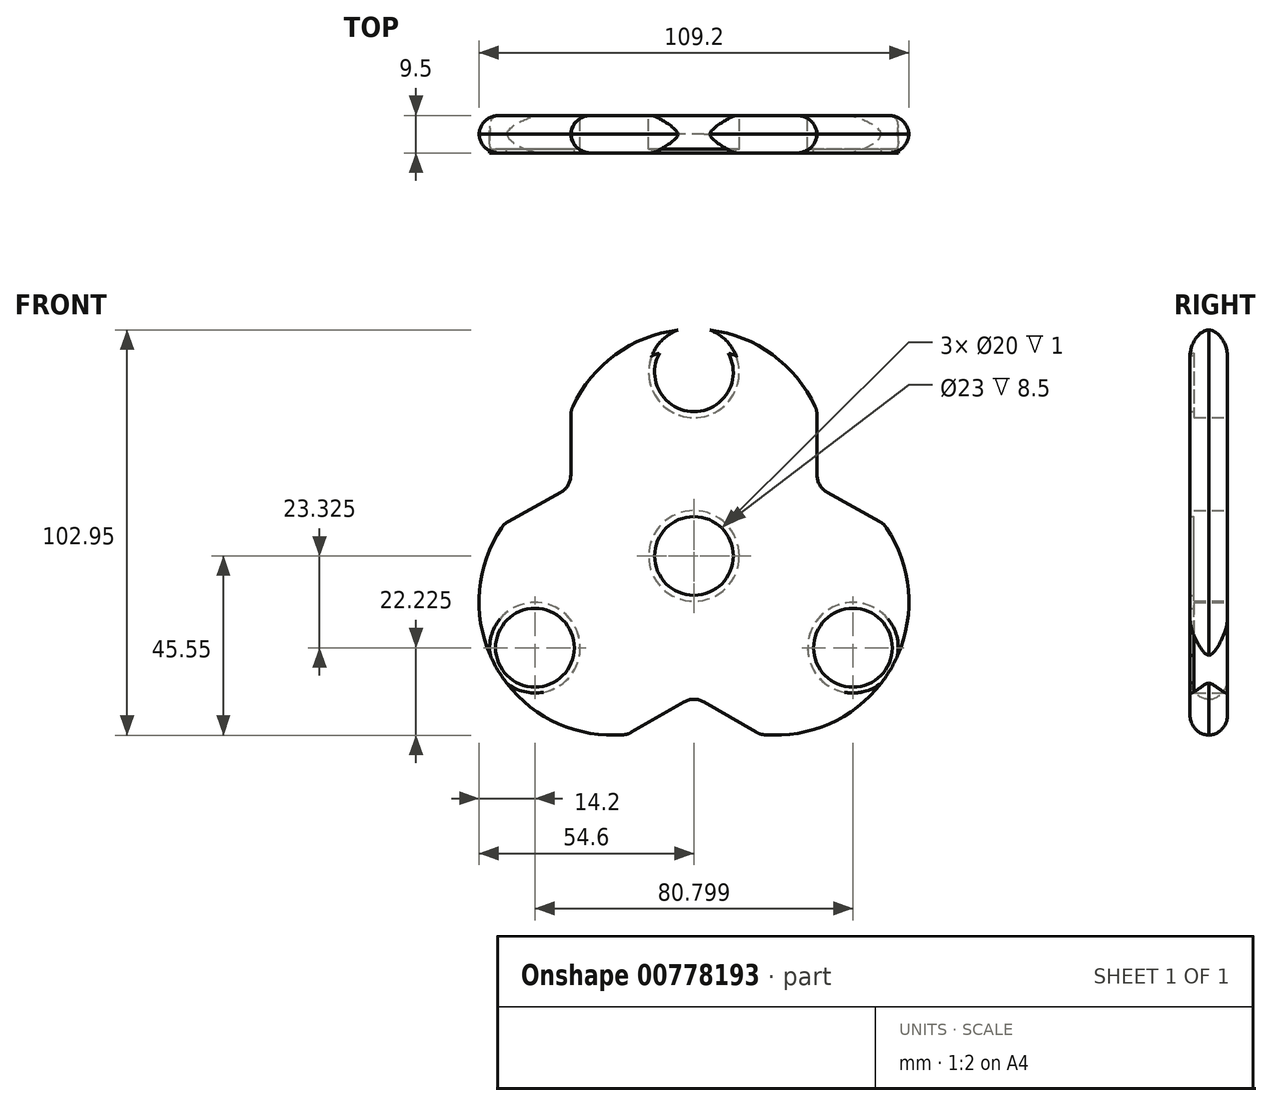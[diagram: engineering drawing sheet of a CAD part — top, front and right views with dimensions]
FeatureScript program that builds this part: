
annotation { "Feature Type Name" : "Feature", "Feature Type Description" : "" }
export const myFeature = defineFeature(function(context is Context, id is Id, definition is map)
    precondition{}
    {
        {
            var Q0;
            Q0=qCreatedBy(makeId("Front.planeOp"),FACE);
            var sketch = newSketch(context, id + "F0", { "sketchPlane" : qUnion([Q0])});
            skCircle(sketch, "E0", {"center": v(0, 0) * mm, "radius": 11.5 * mm});
            skPoint(sketch, "E1", {"position": v(-31.25, 36.9) * mm});
            skPoint(sketch, "E2", {"position": v(31.25, 36.9) * mm});
            skArc(sketch, "E3", {"start": v(30.8, 37.93) * mm, "mid": v(0, 57.65) * mm, "end": v(-30.8, 37.93) * mm});
            skPoint(sketch, "E4", {"position": v(-16.74, -45.31) * mm});
            skPoint(sketch, "E5", {"position": v(16.74, -45.31) * mm});
            skPoint(sketch, "E6", {"position": v(48.18, 8.2) * mm});
            skPoint(sketch, "E7", {"position": v(-48.18, 8.2) * mm});
            skArc(sketch, "E8", {"start": v(-48.9, 7.16) * mm, "mid": v(-49.9, -28.87) * mm, "end": v(-17.9, -45.43) * mm});
            skArc(sketch, "E9", {"start": v(17.9, -45.43) * mm, "mid": v(49.9, -28.87) * mm, "end": v(48.9, 7.16) * mm});
            skPoint(sketch, "E10", {"position": v(0, -35.66) * mm});
            skPoint(sketch, "E11", {"position": v(-31.3, 17.57) * mm});
            skPoint(sketch, "E12", {"position": v(31.3, 17.57) * mm});
            skLineSegment(sketch, "E13", {"start": v(2.5, -37.1) * mm, "end": v(15.8, -44.78) * mm});
            skLineSegment(sketch, "E14", {"start": v(-33.86, 16.15) * mm, "end": v(-47.17, 8.76) * mm});
            skLineSegment(sketch, "E15", {"start": v(-2.5, -37.1) * mm, "end": v(-15.8, -44.78) * mm});
            skLineSegment(sketch, "E16", {"start": v(-31.25, 35.85) * mm, "end": v(-31.29, 20.5) * mm});
            skLineSegment(sketch, "E17", {"start": v(31.25, 35.85) * mm, "end": v(31.29, 20.5) * mm});
            skLineSegment(sketch, "E18", {"start": v(47.17, 8.76) * mm, "end": v(33.86, 16.15) * mm});
            skCircle(sketch, "E19", {"center": v(-40.4, -23.32) * mm, "radius": 11.5 * mm});
            skCircle(sketch, "E20", {"center": v(0, 46.65) * mm, "radius": 11.5 * mm});
            skCircle(sketch, "E21", {"center": v(40.4, -23.32) * mm, "radius": 11.5 * mm});
            skPoint(sketch, "E22", {"position": v(-49.93, -28.82) * mm});
            skPoint(sketch, "E23", {"position": v(0, 57.65) * mm});
            skPoint(sketch, "E24", {"position": v(49.93, -28.82) * mm});
            skArc(sketch, "E25.filletArc", {"start": v(-30.8, 37.93) * mm, "mid": v(-31.13, 36.91) * mm, "end": v(-31.25, 35.85) * mm});
            skArc(sketch, "E26.filletArc", {"start": v(31.25, 35.85) * mm, "mid": v(31.13, 36.91) * mm, "end": v(30.8, 37.93) * mm});
            skArc(sketch, "E27.filletArc", {"start": v(48.9, 7.16) * mm, "mid": v(48.13, 8.06) * mm, "end": v(47.17, 8.76) * mm});
            skArc(sketch, "E28.filletArc", {"start": v(15.8, -44.78) * mm, "mid": v(16.81, -45.22) * mm, "end": v(17.9, -45.43) * mm});
            skArc(sketch, "E29.filletArc", {"start": v(-17.9, -45.43) * mm, "mid": v(-16.81, -45.22) * mm, "end": v(-15.8, -44.78) * mm});
            skArc(sketch, "E30.filletArc", {"start": v(-47.17, 8.76) * mm, "mid": v(-48.13, 8.06) * mm, "end": v(-48.9, 7.16) * mm});
            skArc(sketch, "E31.filletArc", {"start": v(2.5, -37.1) * mm, "mid": v(0, -36.43) * mm, "end": v(-2.5, -37.1) * mm});
            skArc(sketch, "E32.filletArc", {"start": v(31.29, 20.5) * mm, "mid": v(31.98, 17.98) * mm, "end": v(33.86, 16.15) * mm});
            skArc(sketch, "E33.filletArc", {"start": v(-33.86, 16.15) * mm, "mid": v(-31.98, 17.98) * mm, "end": v(-31.29, 20.5) * mm});
            skSolve(sketch);
        }
        {
            var Q0;
            Q0=makeQuery(id+"F0.imprint","IMPRINT",FACE,{"disambiguationData":[TD([[makeQuery(id+"F0.imprint","IMPRINT",EDGE,{"derivedFrom":sQuery(id+"F0.wireOp",EDGE,"E0")}),-1.0]])]});
            extrude(context, id + "F1", {"entities" : qUnion([Q0]), "depth" : 4.75 * mm, "offsetDistance" : 25 * mm});
        }
        {
            var Q0;
            {var subQ0=sQuery(id+"F0.wireOp",EDGE,"E8");Q0=makeQuery(id+"F1.opExtrude","CAP_EDGE",EDGE,{"disambiguationData":[OSD([subQ0]),TDD([makeQuery(id+"F0.imprint","IMPRINT",EDGE,{"disambiguationData":[TD([[makeQuery(id+"F0.imprint","INTERSECT",VERTEX,{"derivedFrom":[subQ0,sQuery(id+"F0.wireOp",EDGE,"E29.filletArc")]}),1.0]])],"derivedFrom":subQ0})])],"isStart":false});}
            var Q1;
            {var subQ0=sQuery(id+"F0.wireOp",EDGE,"E8");Q1=makeQuery(id+"F1.opExtrude","CAP_EDGE",EDGE,{"disambiguationData":[OSD([subQ0]),TDD([makeQuery(id+"F0.imprint","IMPRINT",EDGE,{"disambiguationData":[TD([[makeQuery(id+"F0.imprint","INTERSECT",VERTEX,{"derivedFrom":[subQ0,sQuery(id+"F0.wireOp",EDGE,"E30.filletArc")]}),-1.0]])],"derivedFrom":subQ0})])],"isStart":false});}
            var Q2;
            Q2=makeQuery(id+"F1.opExtrude","CAP_EDGE",EDGE,{"disambiguationData":[OSD([sQuery(id+"F0.wireOp",EDGE,"E17")])],"isStart":false});
            fillet(context, id + "F2", {"entities" : qUnion([Q0, Q1, Q2]), "radius" : 5 * mm, "tangentPropagation" : true, "allowEdgeOverflow" : false});
        }
        {
            var Q0;
            Q0=makeQuery(id+"F1.opExtrude","SWEPT_BODY",BODY,{"disambiguationData":[OSD([sQuery(id+"F0.wireOp",EDGE,"E0"),sQuery(id+"F0.wireOp",EDGE,"E3"),sQuery(id+"F0.wireOp",EDGE,"E8"),sQuery(id+"F0.wireOp",EDGE,"E9"),sQuery(id+"F0.wireOp",EDGE,"E13"),sQuery(id+"F0.wireOp",EDGE,"E14"),sQuery(id+"F0.wireOp",EDGE,"E15"),sQuery(id+"F0.wireOp",EDGE,"E16"),sQuery(id+"F0.wireOp",EDGE,"E17"),sQuery(id+"F0.wireOp",EDGE,"E18"),sQuery(id+"F0.wireOp",EDGE,"E19"),sQuery(id+"F0.wireOp",EDGE,"E20"),sQuery(id+"F0.wireOp",EDGE,"E21"),sQuery(id+"F0.wireOp",EDGE,"E25.filletArc"),sQuery(id+"F0.wireOp",EDGE,"E26.filletArc"),sQuery(id+"F0.wireOp",EDGE,"E27.filletArc"),sQuery(id+"F0.wireOp",EDGE,"E28.filletArc"),sQuery(id+"F0.wireOp",EDGE,"E29.filletArc"),sQuery(id+"F0.wireOp",EDGE,"E30.filletArc"),sQuery(id+"F0.wireOp",EDGE,"E31.filletArc"),sQuery(id+"F0.wireOp",EDGE,"E32.filletArc"),sQuery(id+"F0.wireOp",EDGE,"E33.filletArc")])]});
            var Q1;
            Q1=qCreatedBy(makeId("Front.planeOp"),FACE);
            mirror(context, id + "F3", {"operationType" : NewBodyOperationType.ADD, "entities" : qUnion([Q0]), "mirrorPlane" : qUnion([Q1])});
        }
        {
            var Q0;
            Q0=qCreatedBy(makeId("Front.planeOp"),FACE);
            var sketch = newSketch(context, id + "F4", { "sketchPlane" : qUnion([Q0])});
            skCircle(sketch, "E34.cCircle", {"center": v(0, 0) * mm, "radius": 11.66 * mm, "construction": true});
            skLineSegment(sketch, "E34.0", {"start": v(20.2, -11.66) * mm, "end": v(-20.2, -11.66) * mm});
            skLineSegment(sketch, "E34.1", {"start": v(-20.2, -11.66) * mm, "end": v(0, 23.33) * mm});
            skLineSegment(sketch, "E34.2", {"start": v(0, 23.32) * mm, "end": v(20.2, -11.66) * mm});
            skPoint(sketch, "E34.0.midPoint", {"position": v(0, -11.66) * mm});
            skSolve(sketch);
        }
        {
            var Q0;
            Q0=qCreatedBy(makeId("Front.planeOp"),FACE);
            var sketch = newSketch(context, id + "F5", { "sketchPlane" : qUnion([Q0])});
            skCircle(sketch, "E35", {"center": v(0, 0) * mm, "radius": 11.5 * mm});
            skArc(sketch, "E36", {"start": v(30.8, 37.93) * mm, "mid": v(0, 57.65) * mm, "end": v(-30.8, 37.93) * mm});
            skArc(sketch, "E37", {"start": v(-48.9, 7.16) * mm, "mid": v(-49.9, -28.87) * mm, "end": v(-17.9, -45.43) * mm});
            skArc(sketch, "E38", {"start": v(17.9, -45.43) * mm, "mid": v(49.9, -28.87) * mm, "end": v(48.9, 7.16) * mm});
            skCircle(sketch, "E39", {"center": v(-40.4, -23.32) * mm, "radius": 11.5 * mm});
            skCircle(sketch, "E40", {"center": v(0, 46.65) * mm, "radius": 11.5 * mm});
            skCircle(sketch, "E41", {"center": v(40.4, -23.32) * mm, "radius": 11.5 * mm});
            skPoint(sketch, "E42", {"position": v(-49.93, -28.82) * mm});
            skPoint(sketch, "E43", {"position": v(0, 57.65) * mm});
            skPoint(sketch, "E44", {"position": v(49.93, -28.82) * mm});
            skCircle(sketch, "E45", {"center": v(-40.4, -23.32) * mm, "radius": 10 * mm});
            skCircle(sketch, "E46", {"center": v(0, 0) * mm, "radius": 10 * mm});
            skCircle(sketch, "E47", {"center": v(0, 46.65) * mm, "radius": 10 * mm});
            skCircle(sketch, "E48", {"center": v(40.4, -23.32) * mm, "radius": 10 * mm});
            skArc(sketch, "E49", {"start": v(30.8, 32.93) * mm, "mid": v(0, 52.65) * mm, "end": v(-30.8, 32.93) * mm});
            skPoint(sketch, "E50", {"position": v(0, 52.65) * mm});
            skSolve(sketch);
        }
        {
            var Q0;
            Q0=makeQuery(id+"F5.imprint","IMPRINT",FACE,{"disambiguationData":[TD([[makeQuery(id+"F5.imprint","IMPRINT",EDGE,{"derivedFrom":sQuery(id+"F5.wireOp",EDGE,"E35")}),1.0]])]});
            var Q1;
            Q1=makeQuery(id+"F5.imprint","IMPRINT",FACE,{"disambiguationData":[TD([[makeQuery(id+"F5.imprint","IMPRINT",EDGE,{"derivedFrom":sQuery(id+"F5.wireOp",EDGE,"E47")}),-1.0]])]});
            var Q2;
            Q2=makeQuery(id+"F5.imprint","IMPRINT",FACE,{"disambiguationData":[TD([[makeQuery(id+"F5.imprint","IMPRINT",EDGE,{"derivedFrom":sQuery(id+"F5.wireOp",EDGE,"E45")}),-1.0]])]});
            var Q3;
            Q3=makeQuery(id+"F5.imprint","IMPRINT",FACE,{"disambiguationData":[TD([[makeQuery(id+"F5.imprint","IMPRINT",EDGE,{"derivedFrom":sQuery(id+"F5.wireOp",EDGE,"E48")}),-1.0]])]});
            extrude(context, id + "F6", {"entities" : qUnion([Q0, Q1, Q2, Q3]), "operationType" : NewBodyOperationType.ADD, "depth" : 4.75 * mm, "offsetDistance" : 25 * mm, "hasSecondDirection" : true, "secondDirectionOppositeDirection" : false, "secondDirectionDepth" : (4.75 - 1) * mm});
        }
    });
